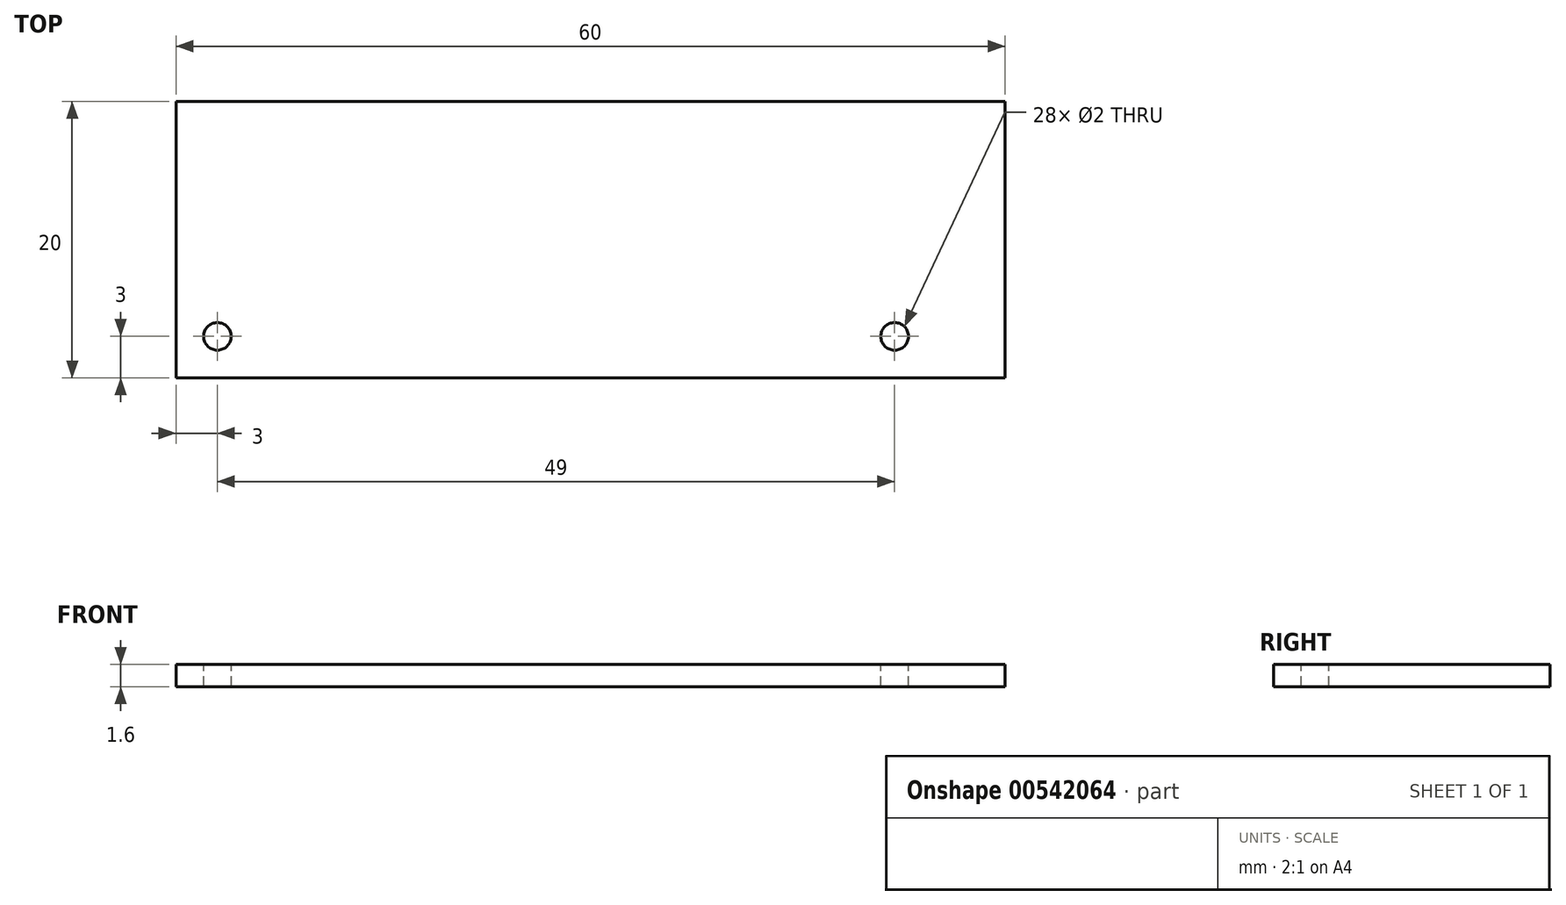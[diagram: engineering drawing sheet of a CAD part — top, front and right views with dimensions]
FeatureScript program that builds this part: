
annotation { "Feature Type Name" : "Feature", "Feature Type Description" : "" }
export const myFeature = defineFeature(function(context is Context, id is Id, definition is map)
    precondition{}
    {
        {
            var Q0;
            Q0=qCreatedBy(makeId("Top.planeOp"),FACE);
            var sketch = newSketch(context, id + "F0", { "sketchPlane" : qUnion([Q0])});
            skLineSegment(sketch, "E0.bottom", {"start": v(30, -10) * mm, "end": v(-30, -10) * mm});
            skLineSegment(sketch, "E0.top", {"start": v(30, 10) * mm, "end": v(-30, 10) * mm});
            skLineSegment(sketch, "E0.left", {"start": v(30, -10) * mm, "end": v(30, 10) * mm});
            skLineSegment(sketch, "E0.right", {"start": v(-30, -10) * mm, "end": v(-30, 10) * mm});
            skPoint(sketch, "E0.middle", {"position": v(0, 0) * mm});
            skSolve(sketch);
        }
        {
            var Q0;
            Q0 = qSketchRegion(id + "F0", true);
            extrude(context, id + "F1", {"entities" : qUnion([Q0]), "depth" : 1.6 * mm, "offsetDistance" : 25 * mm});
        }
        {
            var Q0;
            Q0=makeQuery(id+"F1.opExtrude","CAP_FACE",FACE,{"disambiguationData":[OSD([sQuery(id+"F0.wireOp",EDGE,"E0.bottom"),sQuery(id+"F0.wireOp",EDGE,"E0.top"),sQuery(id+"F0.wireOp",EDGE,"E0.left"),sQuery(id+"F0.wireOp",EDGE,"E0.right")])],"isStart":false});
            var sketch = newSketch(context, id + "F2", { "sketchPlane" : qUnion([Q0])});
            skCircle(sketch, "E1", {"center": v(-27, -7) * mm, "radius": 1 * mm});
            skCircle(sketch, "E2", {"center": v(22, -7) * mm, "radius": 1 * mm});
            skSolve(sketch);
        }
        {
            var Q0;
            Q0 = qSketchRegion(id + "F2", true);
            extrude(context, id + "F3", {"entities" : qUnion([Q0]), "operationType" : NewBodyOperationType.REMOVE, "endBound" : BoundingType.UP_TO_NEXT, "oppositeDirection" : true, "depth" : 25 * mm, "offsetDistance" : 25 * mm});
        }
    });
